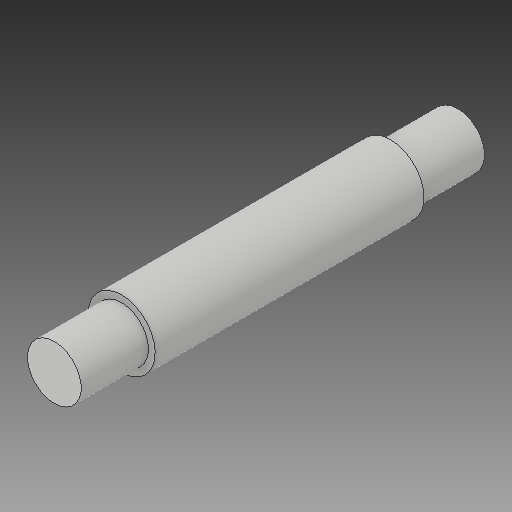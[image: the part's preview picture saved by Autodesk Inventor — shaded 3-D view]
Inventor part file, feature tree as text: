
AUTODESK INVENTOR PART (.ipt)
format: ipt  version: 2019 (Build 230136000, 136)  size: 109,056 bytes
history: native  units: mm
features: revolve x1, sketch x1
ambient origin geometry x8: Origin, YZ Plane, XZ Plane, XY Plane, X Axis, Y Axis, Z Axis, Center Point
bodies: Solid1 (feature_tree)
feature tree (2):
  revolve  "Revolution1"  [1 undecoded]
  sketch  "Sketch1"  dims[d0=4.0mm d1=10.0mm d2=10.0mm d3=5.0mm d4=0.0mm d5=0.0mm d6=40.0mm d7=90.0deg]
note: 1 required parameter value undecoded (feature->parameter linkage not recoverable at this tier; creation-order binding heuristic only, values carry confidence <= 0.55)
